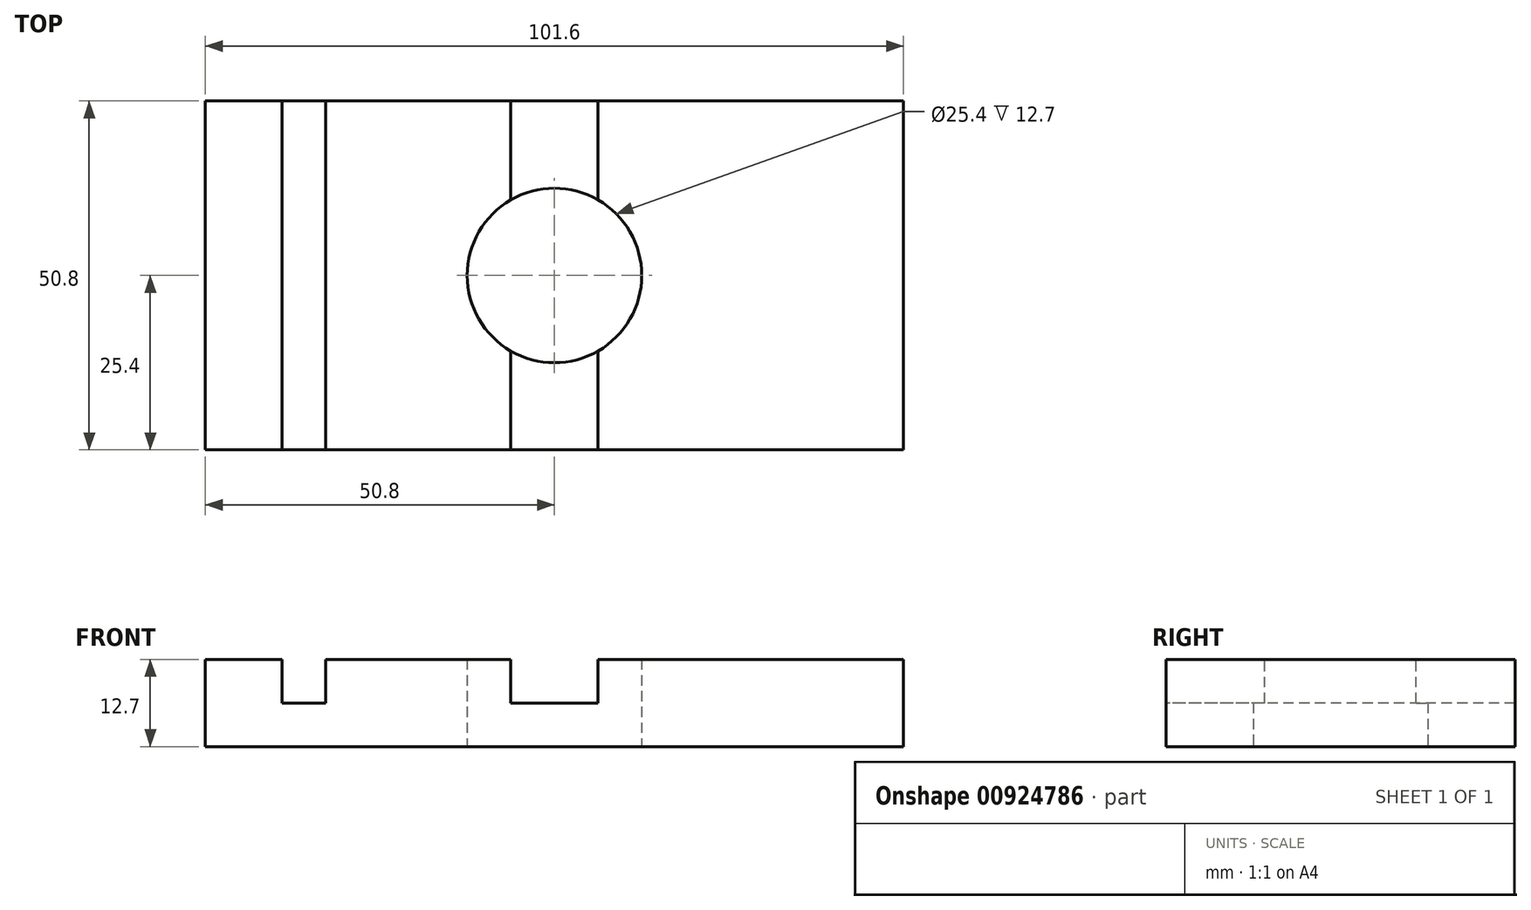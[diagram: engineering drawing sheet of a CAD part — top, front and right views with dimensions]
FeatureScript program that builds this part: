
annotation { "Feature Type Name" : "Feature", "Feature Type Description" : "" }
export const myFeature = defineFeature(function(context is Context, id is Id, definition is map)
    precondition{}
    {
        {
            var Q0;
            Q0=qCreatedBy(makeId("Top.planeOp"),FACE);
            var sketch = newSketch(context, id + "F0", { "sketchPlane" : qUnion([Q0])});
            skLineSegment(sketch, "E0.bottom", {"start": v(50.8, -25.4) * mm, "end": v(-50.8, -25.4) * mm});
            skLineSegment(sketch, "E0.top", {"start": v(50.8, 25.4) * mm, "end": v(-50.8, 25.4) * mm});
            skLineSegment(sketch, "E0.left", {"start": v(50.8, -25.4) * mm, "end": v(50.8, 25.4) * mm});
            skLineSegment(sketch, "E0.right", {"start": v(-50.8, -25.4) * mm, "end": v(-50.8, 25.4) * mm});
            skPoint(sketch, "E0.middle", {"position": v(0, 0) * mm});
            skCircle(sketch, "E1", {"center": v(0, 0) * mm, "radius": 12.7 * mm});
            skSolve(sketch);
        }
        {
            var Q0;
            Q0=makeQuery(id+"F0.imprint","IMPRINT",FACE,{"disambiguationData":[TD([[makeQuery(id+"F0.imprint","IMPRINT",EDGE,{"derivedFrom":sQuery(id+"F0.wireOp",EDGE,"E0.bottom")}),-1.0]])]});
            extrude(context, id + "F1", {"entities" : qUnion([Q0]), "depth" : 12.7 * mm, "offsetDistance" : 25.4 * mm});
        }
        {
            var Q0;
            Q0=makeQuery(id+"F1.opExtrude","CAP_FACE",FACE,{"disambiguationData":[OSD([sQuery(id+"F0.wireOp",EDGE,"E0.bottom"),sQuery(id+"F0.wireOp",EDGE,"E0.top"),sQuery(id+"F0.wireOp",EDGE,"E0.left"),sQuery(id+"F0.wireOp",EDGE,"E0.right"),sQuery(id+"F0.wireOp",EDGE,"E1")])],"isStart":false});
            var sketch = newSketch(context, id + "F2", { "sketchPlane" : qUnion([Q0])});
            skLineSegment(sketch, "E2.bottom", {"start": v(-39.63, 25.4) * mm, "end": v(-33.28, 25.4) * mm});
            skLineSegment(sketch, "E2.top", {"start": v(-39.63, -25.4) * mm, "end": v(-33.28, -25.4) * mm});
            skLineSegment(sketch, "E2.left", {"start": v(-39.63, 25.4) * mm, "end": v(-39.63, -25.4) * mm});
            skLineSegment(sketch, "E2.right", {"start": v(-33.28, 25.4) * mm, "end": v(-33.28, -25.4) * mm});
            skLineSegment(sketch, "E3", {"start": v(-6.35, 25.4) * mm, "end": v(-6.35, -25.4) * mm});
            skLineSegment(sketch, "E4", {"start": v(-6.35, -25.4) * mm, "end": v(6.35, -25.4) * mm});
            skLineSegment(sketch, "E5", {"start": v(6.35, -25.4) * mm, "end": v(6.35, 25.4) * mm});
            skPoint(sketch, "E6", {"position": v(0, 0) * mm});
            skLineSegment(sketch, "E7", {"start": v(-6.35, 25.4) * mm, "end": v(0, 25.4) * mm, "construction": true});
            skLineSegment(sketch, "E8", {"start": v(0, 25.4) * mm, "end": v(0, -25.4) * mm, "construction": true});
            skSolve(sketch);
        }
        {
            var Q0;
            Q0=makeQuery(id+"F2.imprint","IMPRINT",FACE,{"disambiguationData":[TD([[makeQuery(id+"F2.imprint","IMPRINT",EDGE,{"derivedFrom":sQuery(id+"F2.wireOp",EDGE,"E2.bottom")}),1.0]])]});
            var Q1;
            {var subQ0=sQuery(id+"F2.wireOp",EDGE,"E4");Q1=makeQuery(id+"F2.imprint","IMPRINT",FACE,{"disambiguationData":[TD([[makeQuery(id+"F2.imprint","IMPRINT",EDGE,{"derivedFrom":subQ0}),-1.0]])]});}
            var Q2;
            {var subQ0=sQuery(id+"F2.wireOp",EDGE,"E3");var subQ1=makeQuery(id+"F1.opExtrude","CAP_EDGE",EDGE,{"disambiguationData":[OSD([sQuery(id+"F0.wireOp",EDGE,"E0.top")])],"isStart":false});var subQ2=makeQuery(id+"F2.imprint","INTERSECT",VERTEX,{"derivedFrom":[subQ1,subQ0]});Q2=makeQuery(id+"F2.imprint","IMPRINT",FACE,{"disambiguationData":[TD([[makeQuery(id+"F2.imprint","IMPRINT",EDGE,{"disambiguationData":[TD([[subQ2,-1.0]])],"derivedFrom":subQ0}),1.0]])]});}
            extrude(context, id + "F3", {"entities" : qUnion([Q0, Q1, Q2]), "operationType" : NewBodyOperationType.REMOVE, "oppositeDirection" : true, "depth" : 6.35 * mm, "offsetDistance" : 25.4 * mm});
        }
    });
